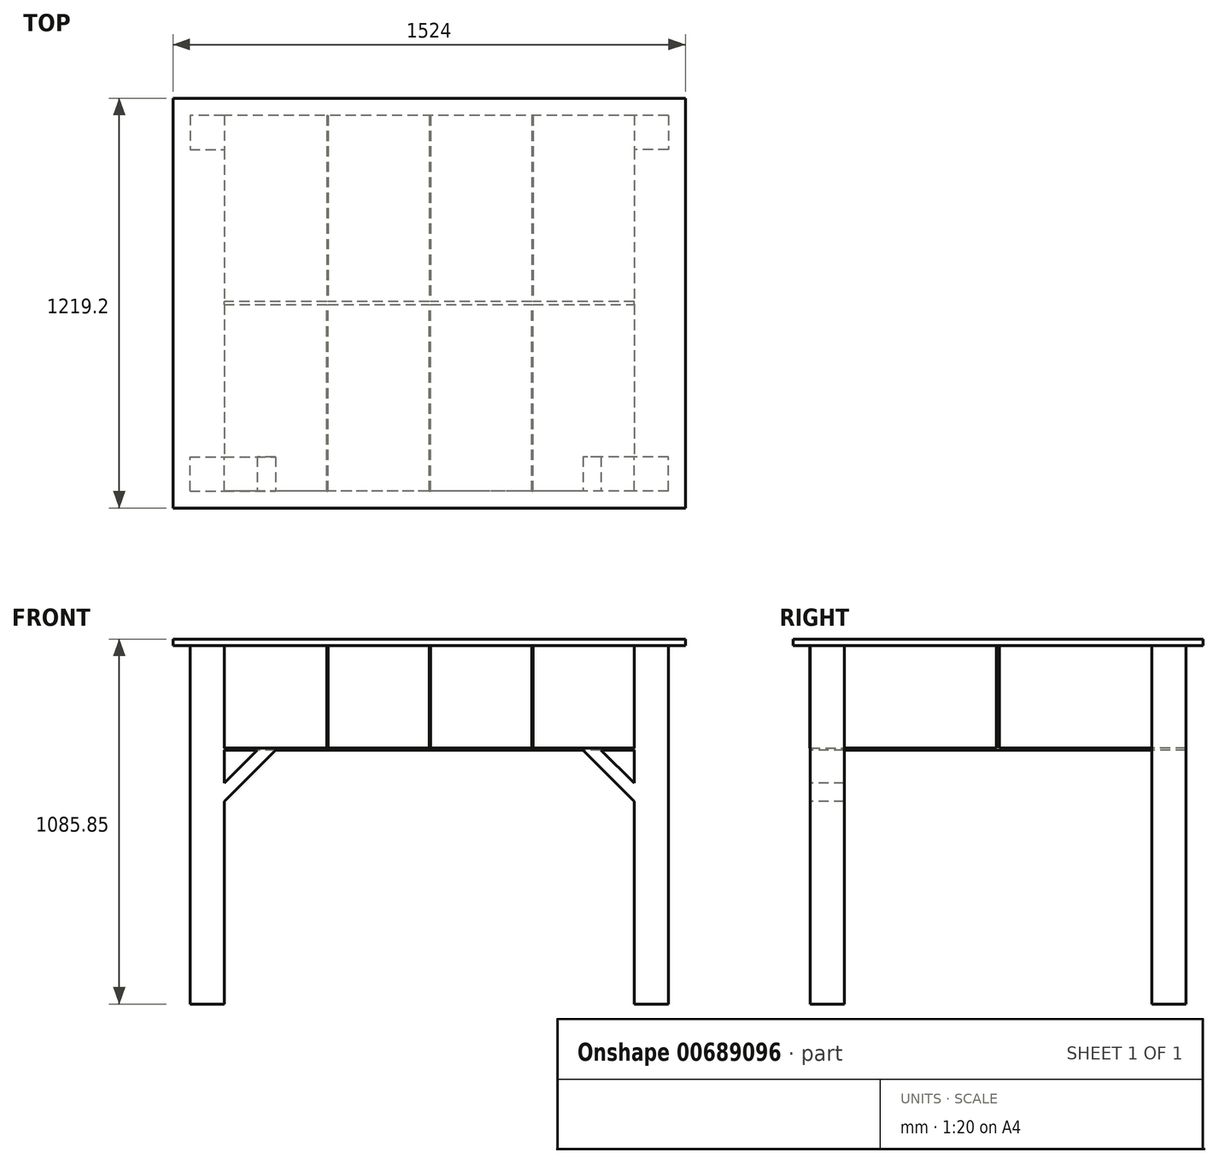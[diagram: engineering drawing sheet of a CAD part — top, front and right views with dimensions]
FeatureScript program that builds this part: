
annotation { "Feature Type Name" : "Feature", "Feature Type Description" : "" }
export const myFeature = defineFeature(function(context is Context, id is Id, definition is map)
    precondition{}
    {
        {
            var Q0;
            Q0=qCreatedBy(makeId("Top.planeOp"),FACE);
            var sketch = newSketch(context, id + "F0", { "sketchPlane" : qUnion([Q0])});
            skLineSegment(sketch, "E0", {"start": v(-844.58, 607.08) * mm, "end": v(679.42, 607.08) * mm});
            skLineSegment(sketch, "E1", {"start": v(679.42, 607.08) * mm, "end": v(679.42, -612.12) * mm});
            skLineSegment(sketch, "E2", {"start": v(679.42, -612.12) * mm, "end": v(-844.58, -612.12) * mm});
            skLineSegment(sketch, "E3", {"start": v(-844.58, -612.12) * mm, "end": v(-844.58, 607.08) * mm});
            skSolve(sketch);
        }
        {
            var Q0;
            Q0=makeQuery(id+"F0.imprint","IMPRINT",FACE,{"disambiguationData":[TD([[makeQuery(id+"F0.imprint","IMPRINT",EDGE,{"derivedFrom":sQuery(id+"F0.wireOp",EDGE,"E0")}),-1.0]])]});
            extrude(context, id + "F1", {"entities" : qUnion([Q0]), "depth" : 19.05 * mm, "offsetDistance" : 25.4 * mm});
        }
        {
            var Q0;
            Q0=makeQuery(id+"F0.imprint","IMPRINT",FACE,{"disambiguationData":[TD([[makeQuery(id+"F0.imprint","IMPRINT",EDGE,{"derivedFrom":sQuery(id+"F0.wireOp",EDGE,"E0")}),-1.0]])]});
            var sketch = newSketch(context, id + "F2", { "sketchPlane" : qUnion([Q0])});
            skLineSegment(sketch, "E4", {"start": v(-793.78, 556.28) * mm, "end": v(-793.78, 454.68) * mm});
            skLineSegment(sketch, "E5", {"start": v(-793.78, 454.68) * mm, "end": v(-692.18, 454.68) * mm});
            skLineSegment(sketch, "E6", {"start": v(-692.18, 454.68) * mm, "end": v(-692.18, 556.28) * mm});
            skLineSegment(sketch, "E7", {"start": v(-692.18, 556.28) * mm, "end": v(-793.78, 556.28) * mm});
            skLineSegment(sketch, "E8.bottom", {"start": v(-793.78, -561.32) * mm, "end": v(-692.18, -561.32) * mm});
            skLineSegment(sketch, "E8.top", {"start": v(-793.78, -459.72) * mm, "end": v(-692.18, -459.72) * mm});
            skLineSegment(sketch, "E8.left", {"start": v(-793.78, -561.32) * mm, "end": v(-793.78, -459.72) * mm});
            skLineSegment(sketch, "E8.right", {"start": v(-692.18, -561.32) * mm, "end": v(-692.18, -459.72) * mm});
            skLineSegment(sketch, "E9.bottom", {"start": v(628.62, 556.28) * mm, "end": v(527.02, 556.28) * mm});
            skLineSegment(sketch, "E9.top", {"start": v(628.62, 454.68) * mm, "end": v(527.02, 454.68) * mm});
            skLineSegment(sketch, "E9.left", {"start": v(628.62, 556.28) * mm, "end": v(628.62, 454.68) * mm});
            skLineSegment(sketch, "E9.right", {"start": v(527.02, 556.28) * mm, "end": v(527.02, 454.68) * mm});
            skPoint(sketch, "E10.startSnap0", {"position": v(628.62, 505.48) * mm});
            skLineSegment(sketch, "E11.bottom", {"start": v(628.62, -561.32) * mm, "end": v(527.02, -561.32) * mm});
            skLineSegment(sketch, "E11.top", {"start": v(628.62, -459.72) * mm, "end": v(527.02, -459.72) * mm});
            skLineSegment(sketch, "E11.left", {"start": v(628.62, -561.32) * mm, "end": v(628.62, -459.72) * mm});
            skLineSegment(sketch, "E11.right", {"start": v(527.02, -561.32) * mm, "end": v(527.02, -459.72) * mm});
            skSolve(sketch);
        }
        {
            var Q0;
            Q0=makeQuery(id+"F2.imprint","IMPRINT",FACE,{"disambiguationData":[TD([[makeQuery(id+"F2.imprint","IMPRINT",EDGE,{"derivedFrom":sQuery(id+"F2.wireOp",EDGE,"E8.bottom")}),1.0]])]});
            var Q1;
            Q1=makeQuery(id+"F2.imprint","IMPRINT",FACE,{"disambiguationData":[TD([[makeQuery(id+"F2.imprint","IMPRINT",EDGE,{"derivedFrom":sQuery(id+"F2.wireOp",EDGE,"E11.bottom")}),-1.0]])]});
            var Q2;
            Q2=makeQuery(id+"F2.imprint","IMPRINT",FACE,{"disambiguationData":[TD([[makeQuery(id+"F2.imprint","IMPRINT",EDGE,{"derivedFrom":sQuery(id+"F2.wireOp",EDGE,"E9.bottom")}),1.0]])]});
            var Q3;
            Q3=makeQuery(id+"F2.imprint","IMPRINT",FACE,{"disambiguationData":[TD([[makeQuery(id+"F2.imprint","IMPRINT",EDGE,{"derivedFrom":sQuery(id+"F2.wireOp",EDGE,"E4")}),1.0]])]});
            extrude(context, id + "F3", {"entities" : qUnion([Q0, Q1, Q2, Q3]), "operationType" : NewBodyOperationType.ADD, "oppositeDirection" : true, "depth" : 1066.8 * mm, "offsetDistance" : 25.4 * mm});
        }
        {
            var Q0;
            Q0=makeQuery(id+"F3.opExtrude","SWEPT_FACE",FACE,{"disambiguationData":[OSD([sQuery(id+"F2.wireOp",EDGE,"E8.right")])]});
            var sketch = newSketch(context, id + "F4", { "sketchPlane" : qUnion([Q0])});
            skLineSegment(sketch, "E12", {"start": v(-561.32, -304.8) * mm, "end": v(-459.72, -304.8) * mm});
            skLineSegment(sketch, "E13", {"start": v(-561.32, -304.8) * mm, "end": v(-561.32, -311.15) * mm});
            skLineSegment(sketch, "E14", {"start": v(-561.32, -311.15) * mm, "end": v(-459.72, -311.15) * mm});
            skLineSegment(sketch, "E15", {"start": v(-459.72, -311.15) * mm, "end": v(-459.72, -304.8) * mm});
            skSolve(sketch);
        }
        {
            var Q0;
            Q0=makeQuery(id+"F4.imprint","IMPRINT",FACE,{"disambiguationData":[TD([[makeQuery(id+"F4.imprint","IMPRINT",EDGE,{"derivedFrom":sQuery(id+"F4.wireOp",EDGE,"E12")}),-1.0]])]});
            extrude(context, id + "F5", {"entities" : qUnion([Q0]), "operationType" : NewBodyOperationType.ADD, "endBound" : BoundingType.UP_TO_NEXT, "depth" : 706.12 * mm, "offsetDistance" : 25.4 * mm});
        }
        {
            var Q0;
            Q0=makeQuery(id+"F5.boolean.opBoolean","MERGE",FACE,{"derivedFrom":[makeQuery(id+"F3.opExtrude","SWEPT_FACE",FACE,{"disambiguationData":[OSD([sQuery(id+"F2.wireOp",EDGE,"E8.top")])]}),makeQuery(id+"F3.opExtrude","SWEPT_FACE",FACE,{"disambiguationData":[OSD([sQuery(id+"F2.wireOp",EDGE,"E11.top")])]}),makeQuery(id+"F5.opExtrude","SWEPT_FACE",FACE,{"disambiguationData":[OSD([sQuery(id+"F4.wireOp",EDGE,"E15")])]})]});
            var sketch = newSketch(context, id + "F6", { "sketchPlane" : qUnion([Q0])});
            skLineSegment(sketch, "E16", {"start": v(-527.02, -304.8) * mm, "end": v(-527.02, -311.15) * mm});
            skLineSegment(sketch, "E17", {"start": v(692.18, -304.8) * mm, "end": v(692.18, -311.15) * mm});
            skSolve(sketch);
        }
        {
            var Q0;
            Q0=makeQuery(id+"F6.imprint","IMPRINT",FACE,{"disambiguationData":[TD([[makeQuery(id+"F6.imprint","IMPRINT",EDGE,{"derivedFrom":sQuery(id+"F6.wireOp",EDGE,"E16")}),1.0]])]});
            extrude(context, id + "F7", {"entities" : qUnion([Q0]), "operationType" : NewBodyOperationType.ADD, "depth" : 1016 * mm, "offsetDistance" : 25.4 * mm});
        }
        {
            var Q0;
            {var subQ0=sQuery(id+"F4.wireOp",EDGE,"E14");Q0=makeQuery(id+"F7.boolean.opBoolean","MERGE",FACE,{"derivedFrom":[makeQuery(id+"F5.opExtrude","SWEPT_FACE",FACE,{"disambiguationData":[OSD([subQ0])]}),makeQuery(id+"F7.opExtrude","SWEPT_FACE",FACE,{"disambiguationData":[OSD([sQuery(id+"F2.wireOp",EDGE,"E8.top"),sQuery(id+"F2.wireOp",EDGE,"E8.right"),subQ0,sQuery(id+"F4.wireOp",EDGE,"E15")])]})]});}
            var sketch = newSketch(context, id + "F8", { "sketchPlane" : qUnion([Q0])});
            skLineSegment(sketch, "E18", {"start": v(-692.18, -2.25) * mm, "end": v(527.02, -2.25) * mm});
            skLineSegment(sketch, "E19", {"start": v(527.02, 7.3) * mm, "end": v(-692.18, 7.3) * mm});
            skLineSegment(sketch, "E20", {"start": v(-692.18, 7.3) * mm, "end": v(-692.18, -2.25) * mm});
            skLineSegment(sketch, "E21", {"start": v(527.02, 7.3) * mm, "end": v(527.02, -2.25) * mm});
            skSolve(sketch);
        }
        {
            var Q0;
            Q0 = qSketchRegion(id + "F8", true);
            extrude(context, id + "F9", {"entities" : qUnion([Q0]), "operationType" : NewBodyOperationType.ADD, "oppositeDirection" : true, "depth" : 311.66 * mm, "offsetDistance" : 25.4 * mm});
        }
        {
            var Q0;
            Q0=makeQuery(id+"F9.opExtrude","SWEPT_FACE",FACE,{"disambiguationData":[OSD([sQuery(id+"F8.wireOp",EDGE,"E19")])]});
            var sketch = newSketch(context, id + "F10", { "sketchPlane" : qUnion([Q0])});
            skLineSegment(sketch, "E22", {"start": v(-387.38, 0) * mm, "end": v(-387.38, -304.8) * mm});
            skLineSegment(sketch, "E23", {"start": v(-387.38, 0) * mm, "end": v(-382.6, 0) * mm});
            skLineSegment(sketch, "E24", {"start": v(-382.6, 0) * mm, "end": v(-382.6, -304.8) * mm});
            skLineSegment(sketch, "E25", {"start": v(-382.6, -304.8) * mm, "end": v(-387.38, -304.8) * mm});
            skLineSegment(sketch, "E26", {"start": v(-82.58, 0) * mm, "end": v(-82.58, -304.8) * mm});
            skLineSegment(sketch, "E27", {"start": v(-82.58, 0) * mm, "end": v(-77.8, 0) * mm});
            skLineSegment(sketch, "E28", {"start": v(-77.8, 0) * mm, "end": v(-77.8, -304.8) * mm});
            skLineSegment(sketch, "E29", {"start": v(-77.8, -304.8) * mm, "end": v(-82.58, -304.8) * mm});
            skLineSegment(sketch, "E30", {"start": v(227, 0) * mm, "end": v(227, -304.8) * mm});
            skLineSegment(sketch, "E31", {"start": v(227, 0) * mm, "end": v(222.22, 0) * mm});
            skLineSegment(sketch, "E32", {"start": v(222.22, 0) * mm, "end": v(222.22, -304.8) * mm});
            skLineSegment(sketch, "E33", {"start": v(222.22, -304.8) * mm, "end": v(227, -304.8) * mm});
            skSolve(sketch);
        }
        {
            var Q0;
            Q0 = qSketchRegion(id + "F10", true);
            extrude(context, id + "F11", {"entities" : qUnion([Q0]), "operationType" : NewBodyOperationType.ADD, "depth" : 554.48 * mm, "offsetDistance" : 25.4 * mm});
        }
        {
            var Q0;
            Q0=makeQuery(id+"F10.imprint","IMPRINT",FACE,{"disambiguationData":[TD([[makeQuery(id+"F10.imprint","IMPRINT",EDGE,{"derivedFrom":sQuery(id+"F10.wireOp",EDGE,"E22")}),1.0]])]});
            var Q1;
            Q1=makeQuery(id+"F10.imprint","IMPRINT",FACE,{"disambiguationData":[TD([[makeQuery(id+"F10.imprint","IMPRINT",EDGE,{"derivedFrom":sQuery(id+"F10.wireOp",EDGE,"E26")}),1.0]])]});
            var Q2;
            Q2=makeQuery(id+"F10.imprint","IMPRINT",FACE,{"disambiguationData":[TD([[makeQuery(id+"F10.imprint","IMPRINT",EDGE,{"derivedFrom":sQuery(id+"F10.wireOp",EDGE,"E30")}),-1.0]])]});
            extrude(context, id + "F12", {"entities" : qUnion([Q0, Q1, Q2]), "operationType" : NewBodyOperationType.ADD, "oppositeDirection" : true, "depth" : 563.12 * mm, "offsetDistance" : 25.4 * mm});
        }
        {
            var Q0;
            Q0=makeQuery(id+"F5.boolean.opBoolean","MERGE",FACE,{"derivedFrom":[makeQuery(id+"F3.opExtrude","SWEPT_FACE",FACE,{"disambiguationData":[OSD([sQuery(id+"F2.wireOp",EDGE,"E8.bottom")])]}),makeQuery(id+"F3.opExtrude","SWEPT_FACE",FACE,{"disambiguationData":[OSD([sQuery(id+"F2.wireOp",EDGE,"E11.bottom")])]}),makeQuery(id+"F5.opExtrude","SWEPT_FACE",FACE,{"disambiguationData":[OSD([sQuery(id+"F4.wireOp",EDGE,"E13")])]})]});
            var sketch = newSketch(context, id + "F13", { "sketchPlane" : qUnion([Q0])});
            skLineSegment(sketch, "E34", {"start": v(-692.44, -463.81) * mm, "end": v(-539.78, -311.15) * mm});
            skPoint(sketch, "E34.endSnap0", {"position": v(-539.78, -304.8) * mm});
            skLineSegment(sketch, "E35", {"start": v(527.02, -463.81) * mm, "end": v(374.36, -311.15) * mm});
            skLineSegment(sketch, "E36", {"start": v(374.36, -311.15) * mm, "end": v(527.02, -311.15) * mm});
            skLineSegment(sketch, "E37", {"start": v(527.02, -311.15) * mm, "end": v(527.02, -463.81) * mm});
            skLineSegment(sketch, "E38", {"start": v(-692.44, -463.81) * mm, "end": v(-692.18, -311.15) * mm});
            skLineSegment(sketch, "E39", {"start": v(-692.18, -311.15) * mm, "end": v(-539.78, -311.15) * mm});
            skLineSegment(sketch, "E40", {"start": v(-692.18, -409.67) * mm, "end": v(-593.66, -311.15) * mm});
            skLineSegment(sketch, "E41", {"start": v(527.02, -409.93) * mm, "end": v(428.24, -311.15) * mm});
            skSolve(sketch);
        }
        {
            var Q0;
            {var subQ0=sQuery(id+"F13.wireOp",EDGE,"E34");var subQ1=sQuery(id+"F4.wireOp",EDGE,"E14");var subQ2=sQuery(id+"F4.wireOp",EDGE,"E13");var subQ3=sQuery(id+"F2.wireOp",EDGE,"E8.right");var subQ4=sQuery(id+"F2.wireOp",EDGE,"E8.bottom");var subQ5=makeQuery(id+"F5.opExtrude","SWEPT_EDGE",EDGE,{"disambiguationData":[OSD([subQ4,subQ3,subQ2,subQ1])]});var subQ6=makeQuery(id+"F13.imprint","INTERSECT",VERTEX,{"derivedFrom":[subQ5,subQ0]});Q0=makeQuery(id+"F13.imprint","IMPRINT",FACE,{"disambiguationData":[TD([[makeQuery(id+"F13.imprint","IMPRINT",EDGE,{"disambiguationData":[TD([[subQ6,1.0]])],"derivedFrom":subQ0}),1.0]])]});}
            extrude(context, id + "F14", {"entities" : qUnion([Q0]), "operationType" : NewBodyOperationType.ADD, "oppositeDirection" : true, "depth" : 101.6 * mm, "offsetDistance" : 25.4 * mm});
        }
        {
            var Q0;
            {var subQ0=sQuery(id+"F13.wireOp",EDGE,"E35");Q0=makeQuery(id+"F13.imprint","IMPRINT",FACE,{"disambiguationData":[TD([[makeQuery(id+"F13.imprint","IMPRINT",EDGE,{"derivedFrom":subQ0}),-1.0]])]});}
            extrude(context, id + "F15", {"entities" : qUnion([Q0]), "operationType" : NewBodyOperationType.ADD, "oppositeDirection" : true, "depth" : 101.6 * mm, "offsetDistance" : 25.4 * mm});
        }
    });
